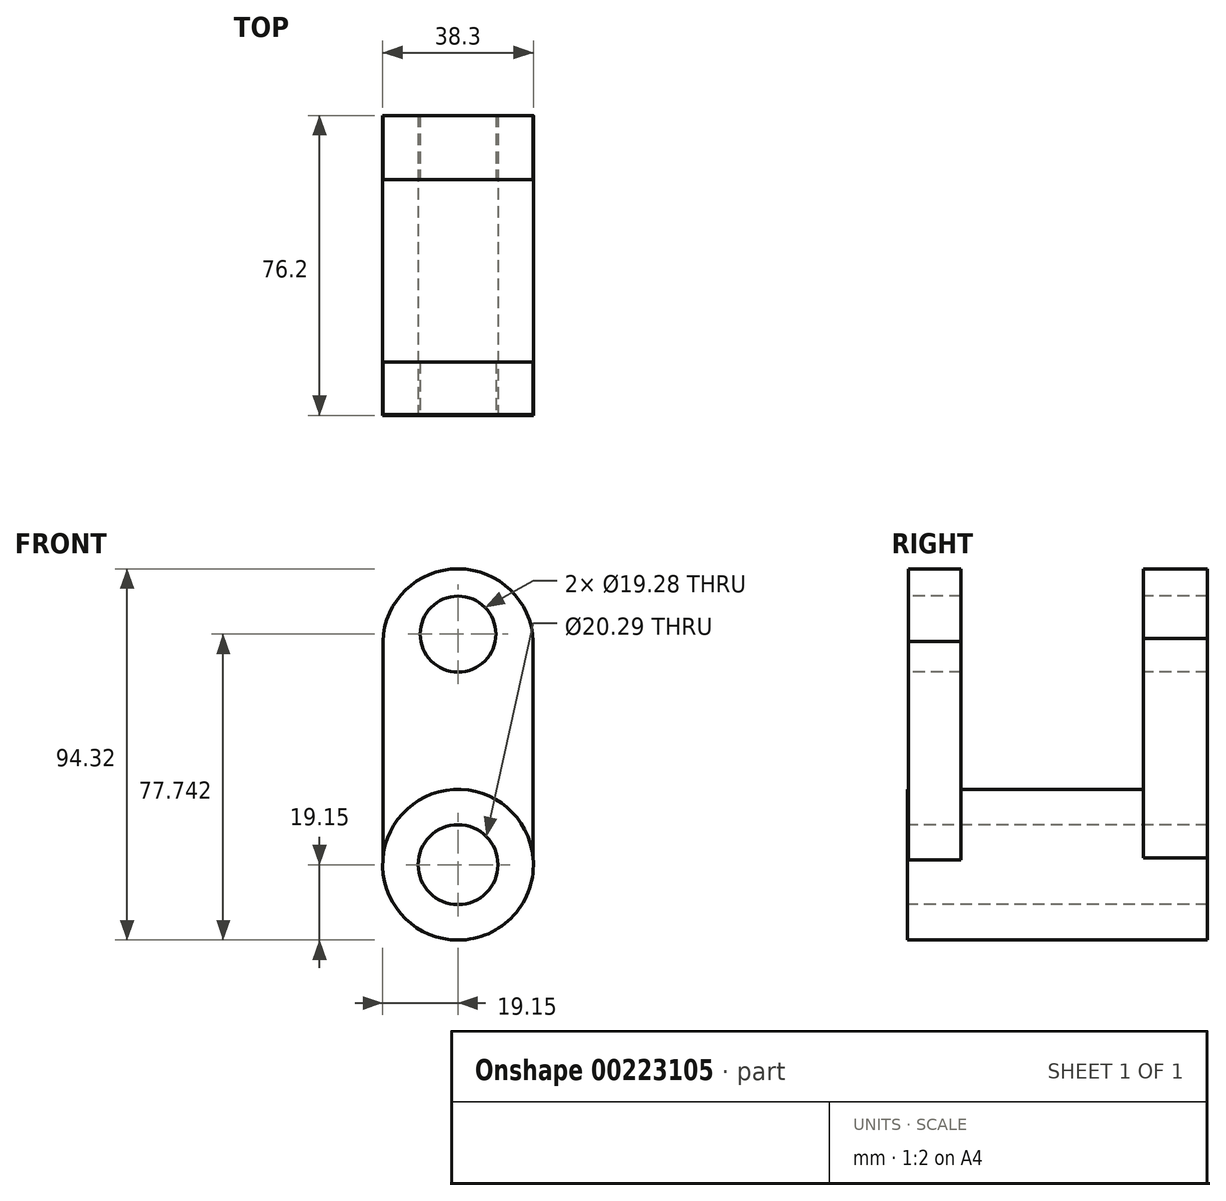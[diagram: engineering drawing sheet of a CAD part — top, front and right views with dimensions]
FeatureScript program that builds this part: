
annotation { "Feature Type Name" : "Feature", "Feature Type Description" : "" }
export const myFeature = defineFeature(function(context is Context, id is Id, definition is map)
    precondition{}
    {
        {
            var Q0;
            Q0=qCreatedBy(makeId("Front.planeOp"),FACE);
            var sketch = newSketch(context, id + "F0", { "sketchPlane" : qUnion([Q0])});
            skCircle(sketch, "E0", {"center": v(0, 0) * mm, "radius": 19.15 * mm});
            skSolve(sketch);
        }
        {
            var Q0;
            Q0 = qSketchRegion(id + "F0", true);
            extrude(context, id + "F1", {"entities" : qUnion([Q0]), "depth" : 76.2 * mm});
        }
        {
            var Q0;
            Q0=makeQuery(id+"F1.opExtrude","CAP_FACE",FACE,{"disambiguationData":[OSD([sQuery(id+"F0.wireOp",EDGE,"E0")])],"isStart":false});
            var sketch = newSketch(context, id + "F2", { "sketchPlane" : qUnion([Q0])});
            skCircle(sketch, "E1", {"center": v(0, 0) * mm, "radius": 10.14 * mm});
            skSolve(sketch);
        }
        {
            var Q0;
            Q0 = qSketchRegion(id + "F2", true);
            extrude(context, id + "F3", {"entities" : qUnion([Q0]), "operationType" : NewBodyOperationType.REMOVE, "oppositeDirection" : true, "depth" : 76.2 * mm});
        }
        {
            var Q0;
            Q0=qCreatedBy(makeId("Top.planeOp"),FACE);
            var sketch = newSketch(context, id + "F4", { "sketchPlane" : qUnion([Q0])});
            skLineSegment(sketch, "E2.bottom", {"start": v(19.07, 0) * mm, "end": v(-19.07, 0) * mm});
            skLineSegment(sketch, "E2.top", {"start": v(19.07, -16.26) * mm, "end": v(-19.07, -16.26) * mm});
            skLineSegment(sketch, "E2.left", {"start": v(19.07, 0) * mm, "end": v(19.07, -16.26) * mm});
            skLineSegment(sketch, "E2.right", {"start": v(-19.07, 0) * mm, "end": v(-19.07, -16.26) * mm});
            skPoint(sketch, "E2.middle", {"position": v(0, -8.13) * mm});
            skSolve(sketch);
        }
        {
            var Q0;
            Q0 = qSketchRegion(id + "F4", true);
            extrude(context, id + "F5", {"entities" : qUnion([Q0]), "operationType" : NewBodyOperationType.ADD, "depth" : 76.2 * mm});
        }
        {
            var Q0;
            Q0=qCreatedBy(makeId("Top.planeOp"),FACE);
            var sketch = newSketch(context, id + "F6", { "sketchPlane" : qUnion([Q0])});
            skLineSegment(sketch, "E3.bottom", {"start": v(-19.11, -62.61) * mm, "end": v(19.11, -62.61) * mm});
            skLineSegment(sketch, "E3.top", {"start": v(-19.11, -76.02) * mm, "end": v(19.11, -76.02) * mm});
            skLineSegment(sketch, "E3.left", {"start": v(-19.11, -62.61) * mm, "end": v(-19.11, -76.02) * mm});
            skLineSegment(sketch, "E3.right", {"start": v(19.11, -62.61) * mm, "end": v(19.11, -76.02) * mm});
            skSolve(sketch);
        }
        {
            var Q0;
            Q0 = qSketchRegion(id + "F6", true);
            extrude(context, id + "F7", {"entities" : qUnion([Q0]), "operationType" : NewBodyOperationType.ADD, "depth" : 76.2 * mm});
        }
        {
            var Q0;
            {var subQ0=sQuery(id+"F6.wireOp",EDGE,"E3.top");Q0=makeQuery(id+"F7.boolean.opBoolean","SPLIT",FACE,{"disambiguationData":[TD([makeQuery(id+"F3.boolean.opBoolean","COPY",FACE,{"derivedFrom":makeQuery(id+"F3.opExtrude","SWEPT_FACE",FACE,{"disambiguationData":[OSD([sQuery(id+"F2.wireOp",EDGE,"E1")])]})})])],"derivedFrom":makeQuery(id+"F7.opExtrude","SWEPT_FACE",FACE,{"disambiguationData":[OSD([subQ0])]})});}
            var sketch = newSketch(context, id + "F8", { "sketchPlane" : qUnion([Q0])});
            skSolve(sketch);
        }
        {
            var Q0;
            {var subQ0=sQuery(id+"F6.wireOp",EDGE,"E3.top");Q0=makeQuery(id+"F8.imprint","IMPRINT",FACE,{"disambiguationData":[TD([[makeQuery(id+"F8.imprint","IMPRINT",EDGE,{"derivedFrom":makeQuery(id+"F7.opExtrude","CAP_EDGE",EDGE,{"disambiguationData":[OSD([subQ0])],"isStart":true})}),1.0]])]});}
            extrude(context, id + "F9", {"entities" : qUnion([Q0]), "operationType" : NewBodyOperationType.REMOVE, "oppositeDirection" : true, "depth" : 127 * mm});
        }
        {
            var Q0;
            {var subQ2=sQuery(id+"F6.wireOp",EDGE,"E3.top");Q0=makeQuery(id+"F7.boolean.opBoolean","SPLIT",FACE,{"disambiguationData":[TD([makeQuery(id+"F1.opExtrude","SWEPT_FACE",FACE,{"disambiguationData":[OSD([sQuery(id+"F0.wireOp",EDGE,"E0")])]})])],"derivedFrom":makeQuery(id+"F7.opExtrude","SWEPT_FACE",FACE,{"disambiguationData":[OSD([subQ2])]})});}
            var sketch = newSketch(context, id + "F10", { "sketchPlane" : qUnion([Q0])});
            skCircle(sketch, "E4", {"center": v(0, 56.05) * mm, "radius": 19.12 * mm});
            skSolve(sketch);
        }
        {
            var Q0;
            {var subQ1=sQuery(id+"F6.wireOp",EDGE,"E3.top");var subQ6=makeQuery(id+"F7.opExtrude","CAP_EDGE",EDGE,{"disambiguationData":[OSD([subQ1])],"isStart":false});Q0=makeQuery(id+"F10.imprint","IMPRINT",FACE,{"disambiguationData":[TD([[makeQuery(id+"F10.imprint","IMPRINT",EDGE,{"derivedFrom":subQ6}),-1.0]])]});}
            extrude(context, id + "F11", {"entities" : qUnion([Q0]), "operationType" : NewBodyOperationType.REMOVE, "oppositeDirection" : true, "depth" : 127 * mm});
        }
        {
            var Q0;
            {var subQ2=sQuery(id+"F6.wireOp",EDGE,"E3.top");Q0=makeQuery(id+"F7.boolean.opBoolean","SPLIT",FACE,{"disambiguationData":[TD([makeQuery(id+"F1.opExtrude","SWEPT_FACE",FACE,{"disambiguationData":[OSD([sQuery(id+"F0.wireOp",EDGE,"E0")])]})])],"derivedFrom":makeQuery(id+"F7.opExtrude","SWEPT_FACE",FACE,{"disambiguationData":[OSD([subQ2])]})});}
            var sketch = newSketch(context, id + "F12", { "sketchPlane" : qUnion([Q0])});
            skCircle(sketch, "E5", {"center": v(0, 58.6) * mm, "radius": 9.64 * mm});
            skSolve(sketch);
        }
        {
            var Q0;
            Q0 = qSketchRegion(id + "F12", true);
            extrude(context, id + "F13", {"entities" : qUnion([Q0]), "operationType" : NewBodyOperationType.REMOVE, "oppositeDirection" : true, "depth" : 127 * mm});
        }
    });
